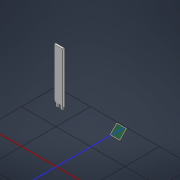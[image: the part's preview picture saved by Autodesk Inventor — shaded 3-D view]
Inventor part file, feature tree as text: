
AUTODESK INVENTOR PART (.ipt)
format: ipt  version: 2021 (Build 250183000, 183)  size: 192,000 bytes
history: native  units: mm
features: extrude x7, sketch x7, reference x6, other x2, plane x1, fillet x1
ambient origin geometry x8: Origin, YZ Plane, XZ Plane, XY Plane, X Axis, Y Axis, Z Axis, Center Point
bodies: Solid1 (feature_tree)
feature tree (24):
  extrude  "Extrusion1"  Depth=0.5mm
  plane  "Work Plane1"
  extrude  "Extrusion2"  TaperAngle=0.0deg  [1 undecoded]
  extrude  "Extrusion3"  Depth=10.0mm
  extrude  "Extrusion4"  Depth=3.0mm TaperAngle=0.0deg
  extrude  "Extrusion5"  TaperAngle=0.0deg  [1 undecoded]
  extrude  "Extrusion6"  Depth=4.0mm
  extrude  "Extrusion7"  TaperAngle=0.0deg  [1 undecoded]
  fillet  "Fillet1"  Radius=0.5mm
  sketch  "Sketch1"  dims[d0=5.0mm d1=0.5mm]
  reference  "Reference1"
  reference  "Reference2"
  sketch  "Sketch2"  dims[d2=150.0mm d3=0.0mm d4=0.0mm d5=0.0mm]
  reference  "Reference3"
  reference  "Reference4"
  reference  "Reference5"
  sketch  "Sketch3"  dims[d6=3.0mm d7=0.0mm d8=10.0mm]
  sketch  "Sketch4"  dims[d9=5.0mm d10=3.0mm d11=0.0mm]
  reference  "Reference6"
  sketch  "Sketch5"  dims[d12=1.0mm d13=0.0mm d14=0.0mm]
  sketch  "Sketch6"  dims[d15=6.666667mm d16=4.0mm]
  sketch  "Sketch9"  dims[d17=0.0mm d18=0.0mm d19=0.0mm d20=0.5mm d21=1.0mm]
  other  "Assembly1"
  other  "Frame"
note: 3 required parameter values undecoded (feature->parameter linkage not recoverable at this tier; creation-order binding heuristic only, values carry confidence <= 0.55)
